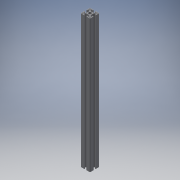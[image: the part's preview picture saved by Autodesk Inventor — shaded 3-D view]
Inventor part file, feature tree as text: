
AUTODESK INVENTOR PART (.ipt)
format: ipt  version: 2018 (Build 220112000, 112)  size: 201,216 bytes
history: native  units: mm
features: other x42, sketch x5, hole x4, extrude x1
ambient origin geometry x8: Origin, YZ Plane, XZ Plane, XY Plane, X Axis, Y Axis, Z Axis, Center Point
bodies: Solid1 (feature_tree)
feature tree (52):
  extrude  "Extrusion1"  [1 undecoded]
  hole  "Drilling 1"  [1 undecoded]
  hole  "Drilling 2"  [1 undecoded]
  hole  "Drilling 3"  [1 undecoded]
  hole  "Drilling 4"  [1 undecoded]
  other  "side_4d_XY"
  other  "side_4d_YZ"
  other  "side_4d_ZX"
  other  "side_4d_X"
  other  "side_4d_Y"
  other  "side_4d_Z"
  other  "side_4d_Center"
  other  "side_1a_XY"
  other  "side_1a_YZ"
  other  "side_1a_ZX"
  other  "side_1a_X"
  other  "side_1a_Y"
  other  "side_1a_Z"
  other  "side_1a_Center"
  other  "side_2b_XY"
  other  "side_2b_YZ"
  other  "side_2b_ZX"
  other  "side_2b_X"
  other  "side_2b_Y"
  other  "side_2b_Z"
  other  "side_2b_Center"
  other  "side_3c_XY"
  other  "side_3c_YZ"
  other  "side_3c_ZX"
  other  "side_3c_X"
  other  "side_3c_Y"
  other  "side_3c_Z"
  other  "side_3c_Center"
  other  "end_XY"
  other  "end_YZ"
  other  "end_ZX"
  other  "end_X"
  other  "end_Y"
  other  "end_Z"
  other  "end_Center"
  other  "start_XY"
  other  "start_YZ"
  other  "start_ZX"
  other  "start_X"
  other  "start_Y"
  other  "start_Z"
  other  "start_Center"
  sketch  "Skizze_1"  dims[d0=569.8mm d1=0.0mm]
  sketch  "Sketch2"  dims[d2=5.0mm d3=6.0mm d4=4.0mm d5=2.0mm d6=90.0deg d7=6000.0mm d8=0.0mm]
  sketch  "Sketch3"  dims[d9=5.0mm d10=6.0mm d11=4.0mm d12=2.0mm d13=90.0deg d14=6000.0mm d15=0.0mm]
  sketch  "Sketch4"  dims[d16=5.0mm d17=6.0mm d18=4.0mm d19=2.0mm d20=90.0deg d21=6000.0mm d22=0.0mm]
  sketch  "Sketch5"  dims[d23=5.0mm d24=6.0mm d25=4.0mm d26=2.0mm d27=90.0deg d28=6000.0mm d29=0.0mm]
note: 5 required parameter values undecoded (feature->parameter linkage not recoverable at this tier; creation-order binding heuristic only, values carry confidence <= 0.55)
